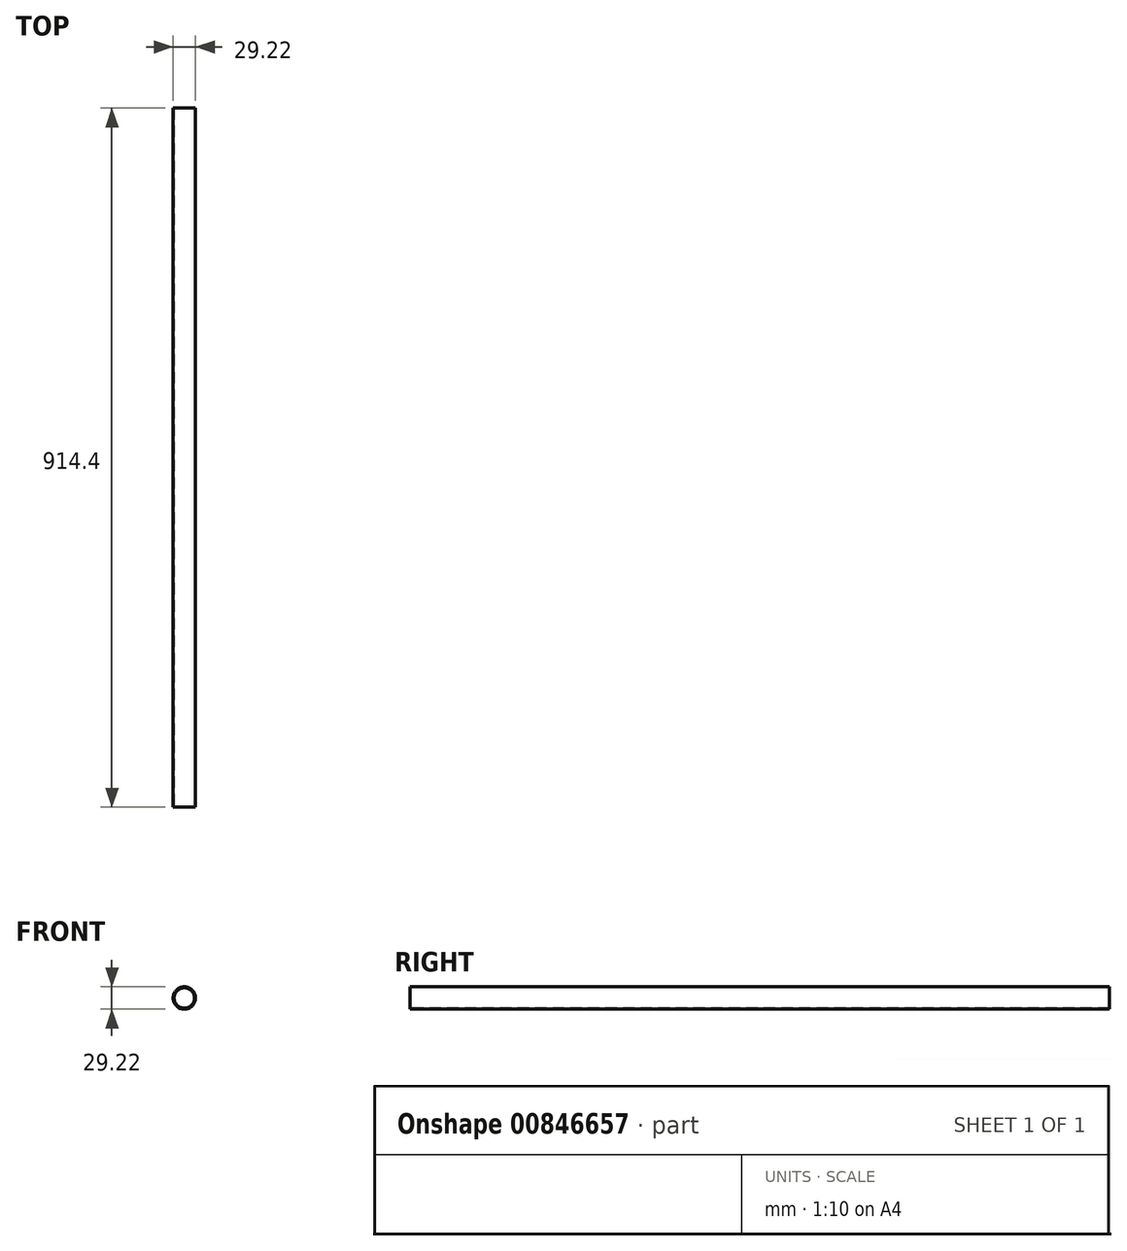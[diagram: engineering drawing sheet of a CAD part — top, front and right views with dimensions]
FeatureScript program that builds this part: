
annotation { "Feature Type Name" : "Feature", "Feature Type Description" : "" }
export const myFeature = defineFeature(function(context is Context, id is Id, definition is map)
    precondition{}
    {
        {
            var Q0;
            Q0=qCreatedBy(makeId("Front.planeOp"),FACE);
            var sketch = newSketch(context, id + "F0", { "sketchPlane" : qUnion([Q0])});
            skCircle(sketch, "E0", {"center": v(0, 0) * mm, "radius": 14.6 * mm});
            skCircle(sketch, "E1", {"center": v(0, 0) * mm, "radius": 13.34 * mm});
            skSolve(sketch);
        }
        {
            var Q0;
            Q0=sQuery(id+"F0.wireOp",EDGE,"E1");
            var Q1;
            Q1=sQuery(id+"F0.wireOp",EDGE,"E0");
            extrude(context, id + "F1", {"bodyType" : ToolBodyType.SURFACE, "surfaceEntities" : qUnion([Q0, Q1]), "endBound" : BoundingType.SYMMETRIC, "depth" : 914.4 * mm, "offsetDistance" : 25.4 * mm, "hasSecondDirection" : true, "secondDirectionOppositeDirection" : true, "secondDirectionDepth" : 25.4 * mm});
        }
    });
